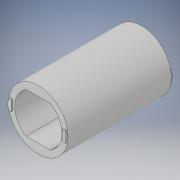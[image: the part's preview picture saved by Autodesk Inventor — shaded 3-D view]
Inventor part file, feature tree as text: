
AUTODESK INVENTOR PART (.ipt)
format: ipt  version: 2017 (Build 210142000, 142)  size: 134,144 bytes
history: native  units: in
note: dims shown in document units (in); Inventor stores cm internally (conversion verified against a paired STEP export)
features: extrude x2, mirror x2, sketch x2
ambient origin geometry x8: Origin, YZ Plane, XZ Plane, XY Plane, X Axis, Y Axis, Z Axis, Center Point
bodies: Solid1 (feature_tree)
feature tree (6):
  extrude  "corridor"  Depth=6.6667in
  extrude  "connection"  Depth=0.25in
  mirror  "mirror plane"
  mirror  "Mirror connetion"
  sketch  "Sketch1"  dims[d0=6.6667in d1=4.0in]
  sketch  "Sketch3"  dims[d2=1.0in d3=17.0in d4=0.0in d7=1.0in d12=0.25in d13=0.0in d20=0.076in d21=0.076in]
